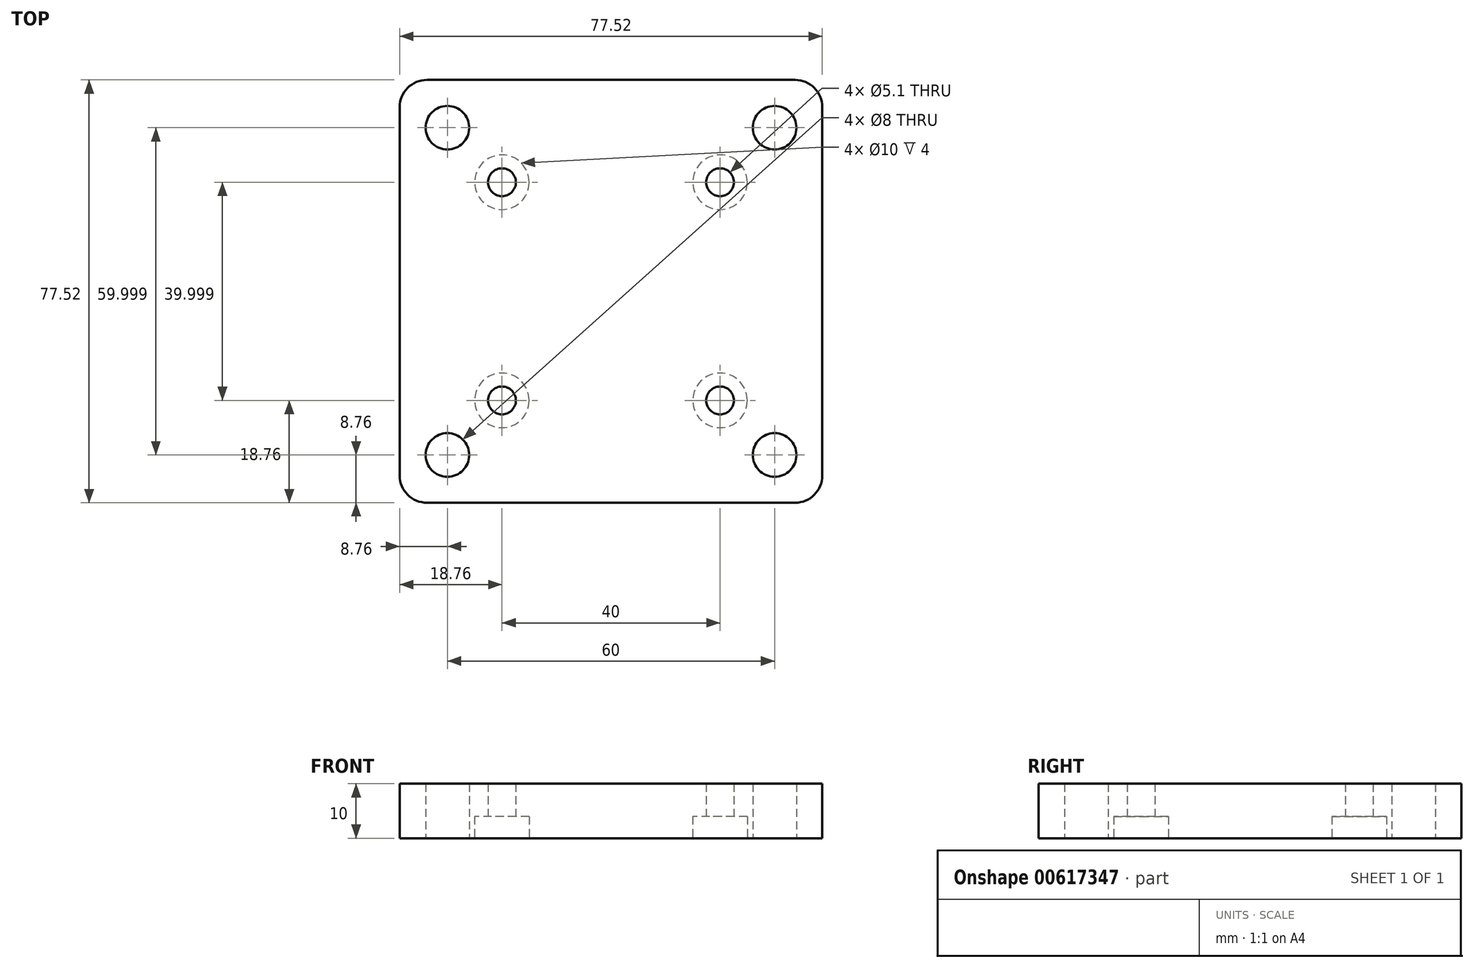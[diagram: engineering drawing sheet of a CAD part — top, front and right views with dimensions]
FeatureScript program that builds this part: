
annotation { "Feature Type Name" : "Feature", "Feature Type Description" : "" }
export const myFeature = defineFeature(function(context is Context, id is Id, definition is map)
    precondition{}
    {
        {
            var Q0;
            Q0=qCreatedBy(makeId("Top.planeOp"),FACE);
            var sketch = newSketch(context, id + "F0", { "sketchPlane" : qUnion([Q0])});
            skLineSegment(sketch, "E0.bottom", {"start": v(38.75, 38.76) * mm, "end": v(-38.76, 38.76) * mm});
            skLineSegment(sketch, "E0.top", {"start": v(38.76, -38.76) * mm, "end": v(-38.76, -38.76) * mm});
            skLineSegment(sketch, "E0.left", {"start": v(38.75, 38.76) * mm, "end": v(38.76, -38.76) * mm});
            skLineSegment(sketch, "E0.right", {"start": v(-38.76, 38.76) * mm, "end": v(-38.75, -38.76) * mm});
            skPoint(sketch, "E0.middle", {"position": v(0, 0) * mm});
            skCircle(sketch, "E1", {"center": v(-30, -30) * mm, "radius": 4 * mm});
            skCircle(sketch, "E2", {"center": v(30, -30) * mm, "radius": 4 * mm});
            skCircle(sketch, "E3", {"center": v(20, -20) * mm, "radius": 2.55 * mm});
            skCircle(sketch, "E4", {"center": v(-20, -20) * mm, "radius": 2.55 * mm});
            skCircle(sketch, "E5", {"center": v(-30, 30) * mm, "radius": 4 * mm});
            skCircle(sketch, "E6", {"center": v(30, 30) * mm, "radius": 4 * mm});
            skCircle(sketch, "E7", {"center": v(20, 20) * mm, "radius": 2.55 * mm});
            skCircle(sketch, "E8", {"center": v(-20, 20) * mm, "radius": 2.55 * mm});
            skCircle(sketch, "E9", {"center": v(-20, 20) * mm, "radius": 5 * mm});
            skCircle(sketch, "E10", {"center": v(20, 20) * mm, "radius": 5 * mm});
            skCircle(sketch, "E11", {"center": v(20, -20) * mm, "radius": 5 * mm});
            skCircle(sketch, "E12", {"center": v(-20, -20) * mm, "radius": 5 * mm});
            skSolve(sketch);
        }
        {
            var Q0;
            Q0=makeQuery(id+"F0.imprint","IMPRINT",FACE,{"disambiguationData":[TD([[makeQuery(id+"F0.imprint","IMPRINT",EDGE,{"derivedFrom":sQuery(id+"F0.wireOp",EDGE,"E0.bottom")}),1.0]])]});
            var Q1;
            Q1=makeQuery(id+"F0.imprint","IMPRINT",FACE,{"disambiguationData":[TD([[makeQuery(id+"F0.imprint","IMPRINT",EDGE,{"derivedFrom":sQuery(id+"F0.wireOp",EDGE,"IMMJGL6N-8Sgl-opJO-aPiA-doJnAwbAfOUA.bottom")}),-1.0]])]});
            var Q2;
            Q2=makeQuery(id+"F0.imprint","IMPRINT",FACE,{"disambiguationData":[TD([[makeQuery(id+"F0.imprint","IMPRINT",EDGE,{"derivedFrom":sQuery(id+"F0.wireOp",EDGE,"E8")}),-1.0]])]});
            var Q3;
            Q3=makeQuery(id+"F0.imprint","IMPRINT",FACE,{"disambiguationData":[TD([[makeQuery(id+"F0.imprint","IMPRINT",EDGE,{"derivedFrom":sQuery(id+"F0.wireOp",EDGE,"E7")}),-1.0]])]});
            var Q4;
            Q4=makeQuery(id+"F0.imprint","IMPRINT",FACE,{"disambiguationData":[TD([[makeQuery(id+"F0.imprint","IMPRINT",EDGE,{"derivedFrom":sQuery(id+"F0.wireOp",EDGE,"E3")}),-1.0]])]});
            var Q5;
            Q5=makeQuery(id+"F0.imprint","IMPRINT",FACE,{"disambiguationData":[TD([[makeQuery(id+"F0.imprint","IMPRINT",EDGE,{"derivedFrom":sQuery(id+"F0.wireOp",EDGE,"E4")}),-1.0]])]});
            extrude(context, id + "F1", {"entities" : qUnion([Q0, Q1, Q2, Q3, Q4, Q5]), "depth" : 10 * mm, "offsetDistance" : 25 * mm});
        }
        {
            var Q0;
            Q0=makeQuery(id+"F1.opExtrude","SWEPT_EDGE",EDGE,{"disambiguationData":[OSD([sQuery(id+"F0.wireOp",EDGE,"E0.top"),sQuery(id+"F0.wireOp",EDGE,"E0.left")])]});
            var Q1;
            Q1=makeQuery(id+"F1.opExtrude","SWEPT_EDGE",EDGE,{"disambiguationData":[OSD([sQuery(id+"F0.wireOp",EDGE,"E0.top"),sQuery(id+"F0.wireOp",EDGE,"E0.right")])]});
            var Q2;
            Q2=makeQuery(id+"F1.opExtrude","SWEPT_EDGE",EDGE,{"disambiguationData":[OSD([sQuery(id+"F0.wireOp",EDGE,"E0.bottom"),sQuery(id+"F0.wireOp",EDGE,"E0.left")])]});
            var Q3;
            Q3=makeQuery(id+"F1.opExtrude","SWEPT_EDGE",EDGE,{"disambiguationData":[OSD([sQuery(id+"F0.wireOp",EDGE,"E0.bottom"),sQuery(id+"F0.wireOp",EDGE,"E0.right")])]});
            fillet(context, id + "F2", {"entities" : qUnion([Q0, Q1, Q2, Q3]), "radius" : 5 * mm, "tangentPropagation" : true, "allowEdgeOverflow" : false});
        }
        {
            var Q0;
            Q0=makeQuery(id+"F0.imprint","IMPRINT",FACE,{"disambiguationData":[TD([[makeQuery(id+"F0.imprint","IMPRINT",EDGE,{"derivedFrom":sQuery(id+"F0.wireOp",EDGE,"E8")}),-1.0]])]});
            var Q1;
            Q1=makeQuery(id+"F0.imprint","IMPRINT",FACE,{"disambiguationData":[TD([[makeQuery(id+"F0.imprint","IMPRINT",EDGE,{"derivedFrom":sQuery(id+"F0.wireOp",EDGE,"E7")}),-1.0]])]});
            var Q2;
            Q2=makeQuery(id+"F0.imprint","IMPRINT",FACE,{"disambiguationData":[TD([[makeQuery(id+"F0.imprint","IMPRINT",EDGE,{"derivedFrom":sQuery(id+"F0.wireOp",EDGE,"E4")}),-1.0]])]});
            var Q3;
            Q3=makeQuery(id+"F0.imprint","IMPRINT",FACE,{"disambiguationData":[TD([[makeQuery(id+"F0.imprint","IMPRINT",EDGE,{"derivedFrom":sQuery(id+"F0.wireOp",EDGE,"E3")}),-1.0]])]});
            extrude(context, id + "F3", {"entities" : qUnion([Q0, Q1, Q2, Q3]), "operationType" : NewBodyOperationType.REMOVE, "depth" : 4 * mm, "offsetDistance" : 25 * mm});
        }
    });
